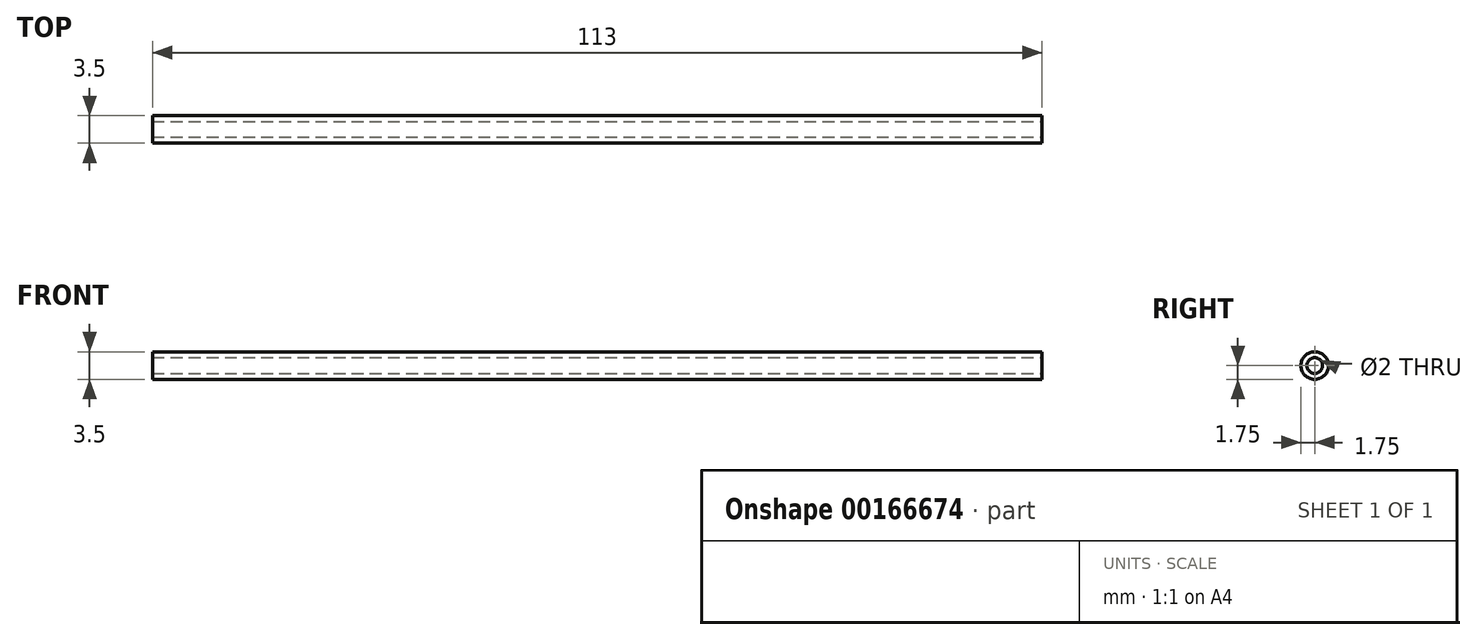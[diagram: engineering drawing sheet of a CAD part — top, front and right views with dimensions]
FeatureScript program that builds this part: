
annotation { "Feature Type Name" : "Feature", "Feature Type Description" : "" }
export const myFeature = defineFeature(function(context is Context, id is Id, definition is map)
    precondition{}
    {
        {
            var Q0;
            Q0=qCreatedBy(makeId("Front.planeOp"),FACE);
            var sketch = newSketch(context, id + "F0", { "sketchPlane" : qUnion([Q0])});
            skLineSegment(sketch, "E0.bottom", {"start": v(0, 1) * mm, "end": v(113, 1) * mm});
            skLineSegment(sketch, "E0.top", {"start": v(0, 1.75) * mm, "end": v(113, 1.75) * mm});
            skLineSegment(sketch, "E0.left", {"start": v(0, 1) * mm, "end": v(0, 1.75) * mm});
            skLineSegment(sketch, "E0.right", {"start": v(113, 1) * mm, "end": v(113, 1.75) * mm});
            skLineSegment(sketch, "E1", {"start": v(0, 0) * mm, "end": v(-6.96, 0) * mm, "construction": true});
            skSolve(sketch);
        }
        {
            var Q0;
            Q0=makeQuery(id+"F0.imprint","IMPRINT",FACE,{"disambiguationData":[TD([[makeQuery(id+"F0.imprint","IMPRINT",EDGE,{"derivedFrom":sQuery(id+"F0.wireOp",EDGE,"E0.bottom")}),1.0]])]});
            var Q1;
            Q1=sQuery(id+"F0.wireOp",EDGE,"E1");
            revolve(context, id + "F1", {"entities" : qUnion([Q0]), "axis" : qUnion([Q1]), "revolveType" : RevolveType.FULL});
        }
    });
